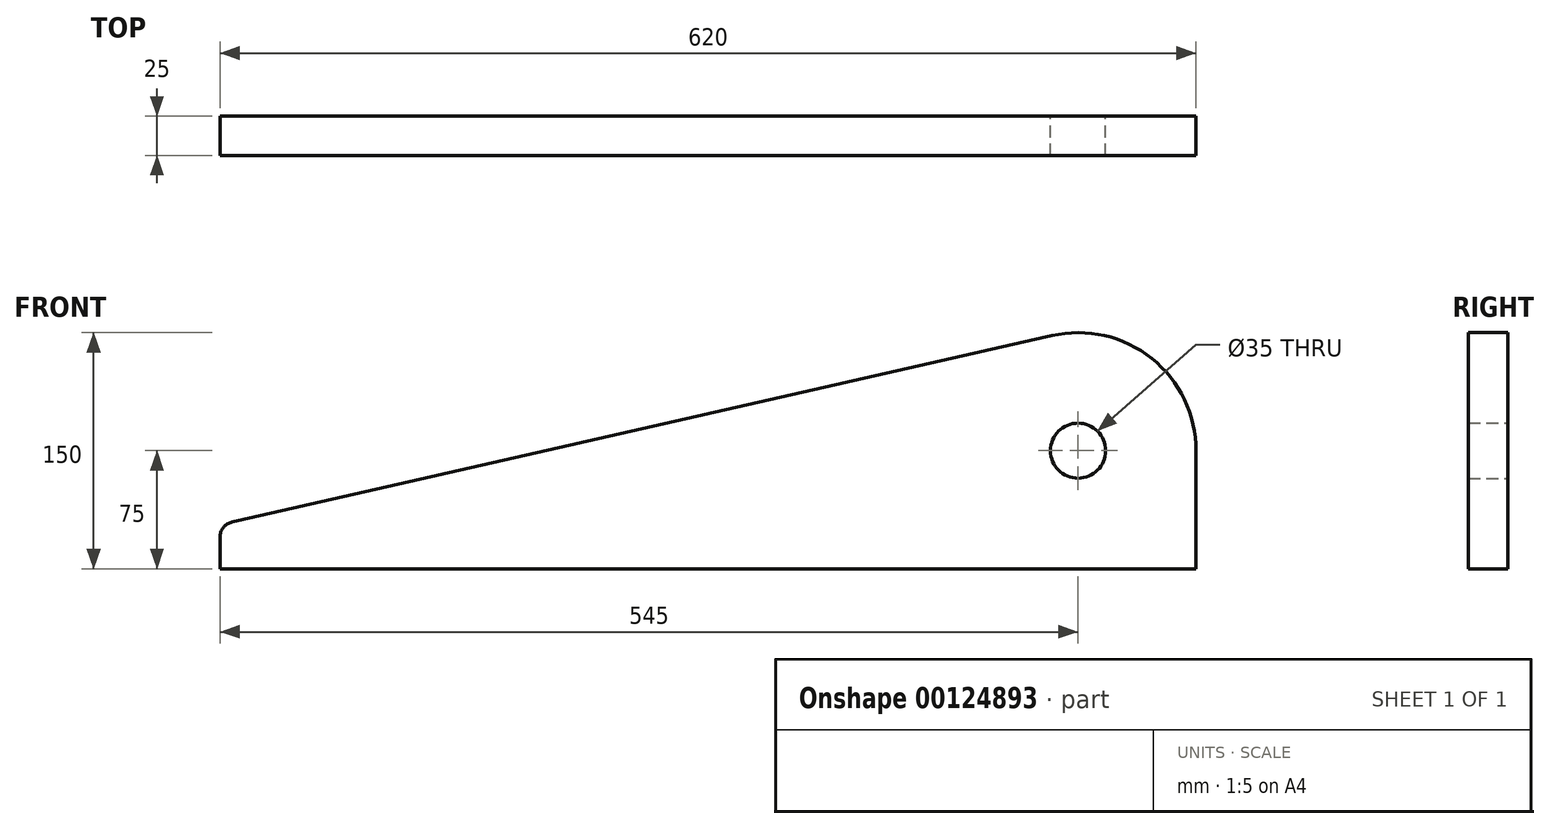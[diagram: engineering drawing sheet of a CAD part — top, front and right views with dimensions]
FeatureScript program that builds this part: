
annotation { "Feature Type Name" : "Feature", "Feature Type Description" : "" }
export const myFeature = defineFeature(function(context is Context, id is Id, definition is map)
    precondition{}
    {
        {
            var Q0;
            Q0=qCreatedBy(makeId("Front.planeOp"),FACE);
            var sketch = newSketch(context, id + "F0", { "sketchPlane" : qUnion([Q0])});
            skLineSegment(sketch, "E0.bottom", {"start": v(0, 0) * mm, "end": v(720, 0) * mm});
            skLineSegment(sketch, "E0.top", {"start": v(0, -20) * mm, "end": v(720, -20) * mm});
            skLineSegment(sketch, "E0.left", {"start": v(0, 0) * mm, "end": v(0, -20) * mm});
            skLineSegment(sketch, "E0.right", {"start": v(720, 0) * mm, "end": v(720, -20) * mm});
            skLineSegment(sketch, "E1", {"start": v(50, 0) * mm, "end": v(50, 20) * mm});
            skLineSegment(sketch, "E2", {"start": v(57.78, 29.75) * mm, "end": v(578.37, 148.13) * mm});
            skArc(sketch, "E3", {"start": v(670, 75) * mm, "mid": v(641.79, 133.62) * mm, "end": v(578.37, 148.13) * mm});
            skLineSegment(sketch, "E4", {"start": v(670, 75) * mm, "end": v(670, 0) * mm});
            skLineSegment(sketch, "E5", {"start": v(595, 150) * mm, "end": v(360.23, 150) * mm});
            skCircle(sketch, "E6", {"center": v(595, 75) * mm, "radius": 17.5 * mm});
            skArc(sketch, "E7", {"start": v(57.78, 29.75) * mm, "mid": v(52.18, 26.24) * mm, "end": v(50, 20) * mm});
            skSolve(sketch);
        }
        {
            var Q0;
            {var subQ3=sQuery(id+"F0.wireOp",EDGE,"E1");Q0=makeQuery(id+"F0.imprint","IMPRINT",FACE,{"disambiguationData":[TD([[makeQuery(id+"F0.imprint","IMPRINT",EDGE,{"derivedFrom":subQ3}),-1.0]])]});}
            extrude(context, id + "F1", {"entities" : qUnion([Q0]), "depth" : 25 * mm});
        }
    });
